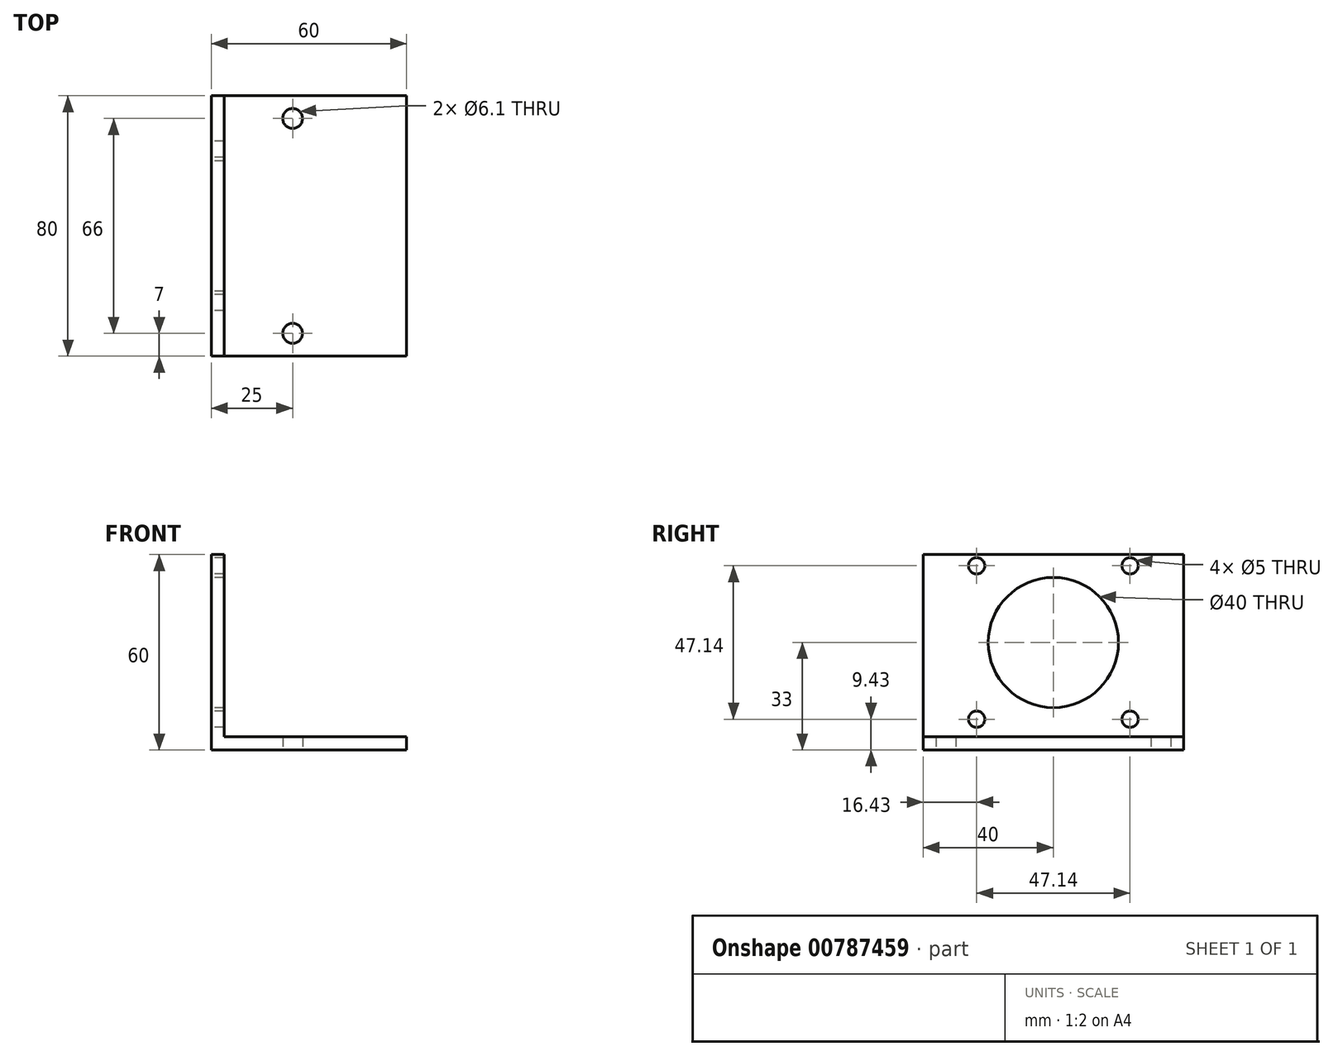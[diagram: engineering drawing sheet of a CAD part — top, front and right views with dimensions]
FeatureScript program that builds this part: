
annotation { "Feature Type Name" : "Feature", "Feature Type Description" : "" }
export const myFeature = defineFeature(function(context is Context, id is Id, definition is map)
    precondition{}
    {
        {
            var Q0;
            Q0=qCreatedBy(makeId("Front.planeOp"),FACE);
            var sketch = newSketch(context, id + "F0", { "sketchPlane" : qUnion([Q0])});
            skLineSegment(sketch, "E0", {"start": v(0, 0) * mm, "end": v(0, 60) * mm});
            skLineSegment(sketch, "E1", {"start": v(0, 60) * mm, "end": v(4, 60) * mm});
            skLineSegment(sketch, "E2", {"start": v(4, 60) * mm, "end": v(4, 4) * mm});
            skLineSegment(sketch, "E3", {"start": v(4, 4) * mm, "end": v(60, 4) * mm});
            skLineSegment(sketch, "E4", {"start": v(60, 4) * mm, "end": v(60, 0) * mm});
            skLineSegment(sketch, "E5", {"start": v(60, 0) * mm, "end": v(0, 0) * mm});
            skSolve(sketch);
        }
        {
            var Q0;
            Q0 = qSketchRegion(id + "F0", true);
            extrude(context, id + "F1", {"entities" : qUnion([Q0]), "depth" : 80 * mm, "offsetDistance" : 25 * mm});
        }
        {
            var Q0;
            Q0=makeQuery(id+"F1.opExtrude","SWEPT_FACE",FACE,{"disambiguationData":[OSD([sQuery(id+"F0.wireOp",EDGE,"E0")])]});
            var sketch = newSketch(context, id + "F2", { "sketchPlane" : qUnion([Q0])});
            skLineSegment(sketch, "E6", {"start": v(40, 60) * mm, "end": v(40, 0) * mm, "construction": true});
            skLineSegment(sketch, "E7", {"start": v(0, 33) * mm, "end": v(80, 33) * mm, "construction": true});
            skPoint(sketch, "E8.middle", {"position": v(40, 33) * mm});
            skCircle(sketch, "E9", {"center": v(16.43, 56.57) * mm, "radius": 2.5 * mm});
            skCircle(sketch, "E10", {"center": v(40, 33) * mm, "radius": 20 * mm});
            skCircle(sketch, "E11.MirrorC", {"center": v(63.57, 56.57) * mm, "radius": 2.5 * mm});
            skCircle(sketch, "E12.MirrorC", {"center": v(16.43, 9.43) * mm, "radius": 2.5 * mm});
            skCircle(sketch, "E13.MirrorC", {"center": v(63.57, 9.43) * mm, "radius": 2.5 * mm});
            skSolve(sketch);
        }
        {
            var Q0;
            Q0=makeQuery(id+"F1.opExtrude","SWEPT_FACE",FACE,{"disambiguationData":[OSD([sQuery(id+"F0.wireOp",EDGE,"E5")])]});
            var sketch = newSketch(context, id + "F3", { "sketchPlane" : qUnion([Q0])});
            skLineSegment(sketch, "E14", {"start": v(25, 80) * mm, "end": v(25, 0) * mm, "construction": true});
            skCircle(sketch, "E15", {"center": v(25, 73) * mm, "radius": 3.05 * mm});
            skCircle(sketch, "E16", {"center": v(25, 7) * mm, "radius": 3.05 * mm});
            skSolve(sketch);
        }
        {
            var Q0;
            Q0 = qSketchRegion(id + "F3", true);
            extrude(context, id + "F4", {"entities" : qUnion([Q0]), "operationType" : NewBodyOperationType.REMOVE, "oppositeDirection" : true, "depth" : 25 * mm, "offsetDistance" : 25 * mm});
        }
        {
            var Q0;
            Q0 = qSketchRegion(id + "F2", true);
            extrude(context, id + "F5", {"entities" : qUnion([Q0]), "operationType" : NewBodyOperationType.REMOVE, "endBound" : BoundingType.UP_TO_NEXT, "oppositeDirection" : true, "depth" : 25 * mm, "offsetDistance" : 25 * mm});
        }
    });
